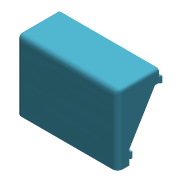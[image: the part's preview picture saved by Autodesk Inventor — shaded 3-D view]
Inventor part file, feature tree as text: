
AUTODESK INVENTOR PART (.ipt)
format: ipt  version: 2020 (Build 240168000, 168)  size: 660,480 bytes
history: native  units: in
note: dims shown in document units (in); Inventor stores cm internally (conversion verified against a paired STEP export)
features: reference x19, sketch x7, extrude x6, other x6, chamfer x4, plane x3, fillet x1, shell x1, helix x1, pattern_linear x1, mirror x1, projected_geometry x1
ambient origin geometry x8: Origin, YZ Plane, XZ Plane, XY Plane, X Axis, Y Axis, Z Axis, Center Point
bodies: Solid1 (feature_tree)
feature tree (51):
  sketch  "Sketch1"  dims[d0=1.0in d1=0.0in d2=0.1875in d3=0.0in d4=0.0in]
  plane  "Work Plane1"
  extrude  "Extrusion1"  Depth=0.1875in
  fillet  "Fillet1"  [1 undecoded]
  extrude  "Extrusion2"  Depth=0.25in TaperAngle=0.0deg
  shell  "Shell1"  Thickness=0.089in
  extrude  "Extrusion3"  Depth=0.0125in TaperAngle=45.0deg
  extrude  "Extrusion4"  Depth=0.0063in
  chamfer  "Chamfer1"  Distance=0.025in
  plane  "Work Plane2"
  helix  "Coil1"  [1 undecoded]
  pattern_linear  "Rectangular Pattern1"  Spacing1=0.025in  [1 undecoded]
  other  "Lip1"
  other  "Lip2"
  extrude  "Extrusion5"  Depth=0.1in
  chamfer  "Chamfer2"  Distance=0.025in
  extrude  "Extrusion6"  Depth=0.1in
  plane  "Work Plane3"
  mirror  "Mirror1"
  chamfer  "Chamfer3"  [1 undecoded]
  chamfer  "Chamfer4"  Distance=0.1in Angle=45.0deg
  reference  "Reference1"
  reference  "Reference4"
  reference  "Reference5"
  reference  "Reference6"
  sketch  "Sketch2"  dims[d5=0.125in d6=0.25in d7=0.0in d8=0.089in]
  reference  "Reference7"
  reference  "Reference8"
  sketch  "Sketch3"  dims[d9=0.25in d10=0.0in d11=0.0125in d12=0.125in d13=45.0deg]
  reference  "Reference9"
  reference  "Reference10"
  reference  "Reference11"
  sketch  "Sketch4"  dims[d14=0.0188in d15=0.0063in]
  reference  "Reference12"
  reference  "Reference13"
  sketch  "Sketch5"  dims[d16=60.0deg]
  projected_geometry  "Projected Loop1"
  sketch  "Sketch6"  dims[d17=0.2687in d18=0.025in d19=0.2687in]
  reference  "Reference14"
  reference  "Reference15"
  reference  "Reference16"
  reference  "Reference17"
  reference  "Reference18"
  reference  "Reference19"
  reference  "Reference20"
  reference  "Reference21"
  sketch  "Sketch7"  dims[d20=0.3937in d21=0.0in d22=90.0deg d23=90.0deg d24=0.0in d25=0.0in d27=0.7874in d29=4.125in d30=0.05in d31=0.0197in d32=0.0in d33=0.0in d34=0.0in d35=0.0in d36=0.05in d37=0.0197in d38=0.0in d39=0.0in d40=0.0in d41=0.0in d42=0.025in d43=0.175in d44=0.025in d45=0.175in d47=0.0in d48=0.1in d49=0.125in d50=45.0deg d51=0.065in d52=0.0in d53=0.045in d54=0.125in d55=45.0deg d56=0.1125in d57=0.1125in d58=0.1in d59=0.125in d60=45.0deg]
  other  "Readout.iam"
  other  "Base2:1"
  other  "Faceplate:1"
  other  "4x20 LCD:2"
note: 4 required parameter values undecoded (feature->parameter linkage not recoverable at this tier; creation-order binding heuristic only, values carry confidence <= 0.55)
